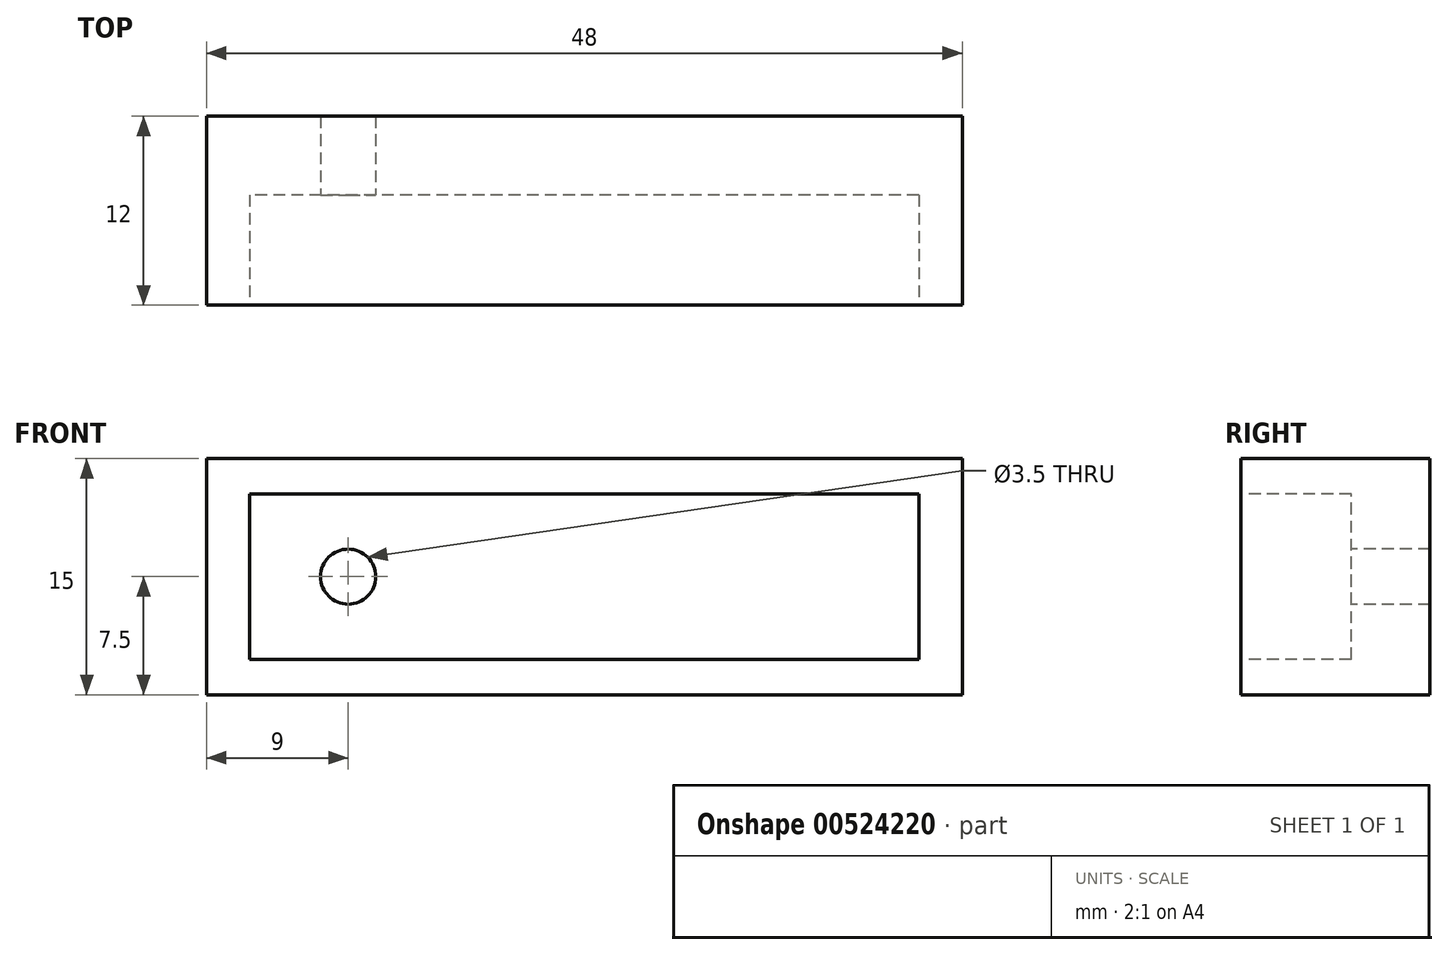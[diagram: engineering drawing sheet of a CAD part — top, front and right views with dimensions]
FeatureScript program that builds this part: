
annotation { "Feature Type Name" : "Feature", "Feature Type Description" : "" }
export const myFeature = defineFeature(function(context is Context, id is Id, definition is map)
    precondition{}
    {
        {
            var Q0;
            Q0=qCreatedBy(makeId("Front.planeOp"),FACE);
            var sketch = newSketch(context, id + "F0", { "sketchPlane" : qUnion([Q0])});
            skLineSegment(sketch, "E0.bottom", {"start": v(-24, 7.5) * mm, "end": v(24, 7.5) * mm});
            skLineSegment(sketch, "E0.top", {"start": v(-24, -7.5) * mm, "end": v(24, -7.5) * mm});
            skLineSegment(sketch, "E0.left", {"start": v(-24, 7.5) * mm, "end": v(-24, -7.5) * mm});
            skLineSegment(sketch, "E0.right", {"start": v(24, 7.5) * mm, "end": v(24, -7.5) * mm});
            skSolve(sketch);
        }
        {
            var Q0;
            Q0=makeQuery(id+"F0.imprint","IMPRINT",FACE,{"disambiguationData":[TD([[makeQuery(id+"F0.imprint","IMPRINT",EDGE,{"derivedFrom":sQuery(id+"F0.wireOp",EDGE,"E0.bottom")}),-1.0]])]});
            extrude(context, id + "F1", {"entities" : qUnion([Q0]), "depth" : 12 * mm, "offsetDistance" : 25 * mm});
        }
        {
            var Q0;
            Q0=makeQuery(id+"F1.opExtrude","CAP_FACE",FACE,{"disambiguationData":[OSD([sQuery(id+"F0.wireOp",EDGE,"E0.bottom"),sQuery(id+"F0.wireOp",EDGE,"E0.top"),sQuery(id+"F0.wireOp",EDGE,"E0.left"),sQuery(id+"F0.wireOp",EDGE,"E0.right")])],"isStart":false});
            var sketch = newSketch(context, id + "F2", { "sketchPlane" : qUnion([Q0])});
            skLineSegment(sketch, "E1.bottom", {"start": v(21.25, -5.25) * mm, "end": v(-21.25, -5.25) * mm});
            skLineSegment(sketch, "E1.top", {"start": v(21.25, 5.25) * mm, "end": v(-21.25, 5.25) * mm});
            skLineSegment(sketch, "E1.left", {"start": v(21.25, -5.25) * mm, "end": v(21.25, 5.25) * mm});
            skLineSegment(sketch, "E1.right", {"start": v(-21.25, -5.25) * mm, "end": v(-21.25, 5.25) * mm});
            skSolve(sketch);
        }
        {
            var Q0;
            Q0=makeQuery(id+"F2.imprint","IMPRINT",FACE,{"disambiguationData":[TD([[makeQuery(id+"F2.imprint","IMPRINT",EDGE,{"derivedFrom":sQuery(id+"F2.wireOp",EDGE,"E1.bottom")}),-1.0]])]});
            extrude(context, id + "F3", {"entities" : qUnion([Q0]), "operationType" : NewBodyOperationType.REMOVE, "oppositeDirection" : true, "depth" : 7 * mm, "offsetDistance" : 25 * mm});
        }
        {
            var Q0;
            Q0=makeQuery(id+"F3.boolean.opBoolean","COPY",FACE,{"derivedFrom":makeQuery(id+"F3.opExtrude","CAP_FACE",FACE,{"disambiguationData":[OSD([sQuery(id+"F2.wireOp",EDGE,"E1.bottom"),sQuery(id+"F2.wireOp",EDGE,"E1.top"),sQuery(id+"F2.wireOp",EDGE,"E1.left"),sQuery(id+"F2.wireOp",EDGE,"E1.right")])],"isStart":false})});
            var sketch = newSketch(context, id + "F4", { "sketchPlane" : qUnion([Q0])});
            skCircle(sketch, "E2", {"center": v(-15, 0) * mm, "radius": 1.75 * mm});
            skSolve(sketch);
        }
        {
            var Q0;
            Q0=makeQuery(id+"F4.imprint","IMPRINT",FACE,{"disambiguationData":[TD([[makeQuery(id+"F4.imprint","IMPRINT",EDGE,{"derivedFrom":sQuery(id+"F4.wireOp",EDGE,"E2")}),1.0]])]});
            extrude(context, id + "F5", {"entities" : qUnion([Q0]), "operationType" : NewBodyOperationType.REMOVE, "endBound" : BoundingType.UP_TO_NEXT, "oppositeDirection" : true, "depth" : 25 * mm, "offsetDistance" : 25 * mm});
        }
    });
